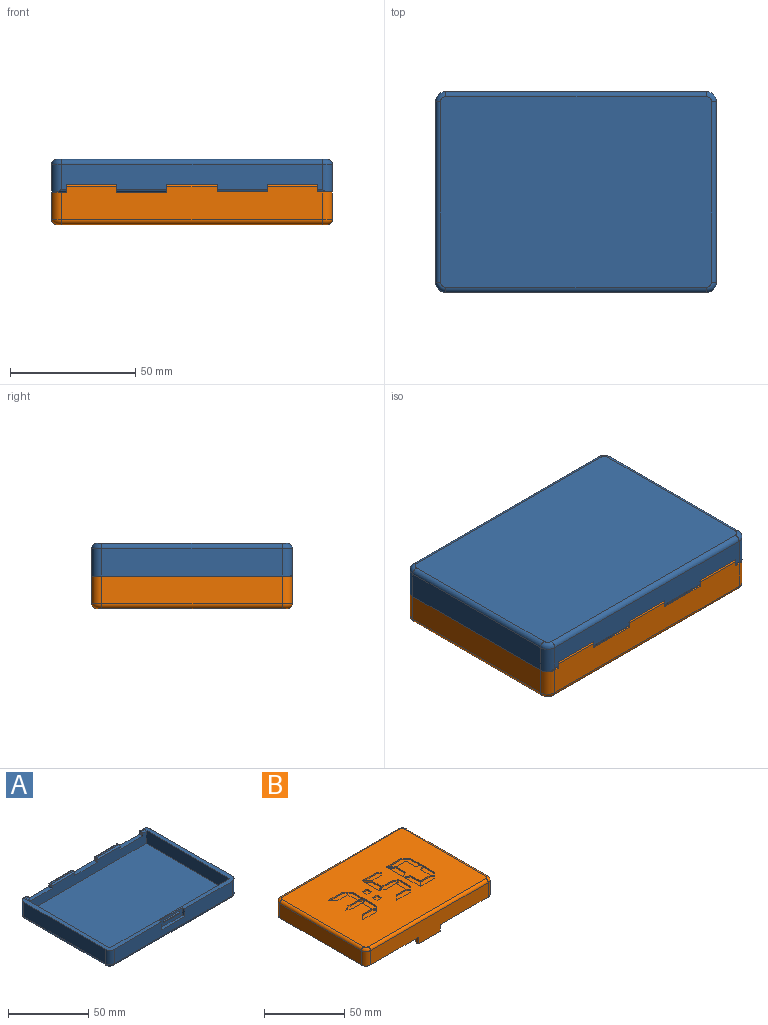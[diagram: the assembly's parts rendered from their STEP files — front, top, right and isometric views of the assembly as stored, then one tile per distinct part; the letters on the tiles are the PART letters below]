
ASSEMBLY  parts=2 mates=1
PART A: 63 faces, bbox 112.7x80.7x13 mm
  f0: plane 104x11mm, normal (0,-1,0), area 1024mm2, adj f1,f7,f8,f50,f54,f55,f62
  f1: plane 112x79mm, normal (0,0,1), area 748.6mm2, adj f0,f5,f6,f7,f8,f9,f10,f12
  f2: plane 20x1mm, normal (0,0,1), area 20mm2, adj f20,f24,f38,f41
  f3: plane 20x1mm, normal (0,0,1), area 20mm2, adj f17,f21,f39,f42
  f4: plane 104x10mm, normal (0,1,0), area 920mm2, adj f5,f10,f17,f18,f19,f20,f21,f22
  f5: cylinder r=4mm len=11mm, axis (0,0,-1), area 68mm2, adj f1,f4,f6,f45,f47
  f6: plane 72x11mm, normal (-1,0,0), area 792mm2, adj f1,f5,f7,f46
  f7: cylinder r=4mm len=11mm, axis (0,0,-1), area 69.1mm2, adj f0,f1,f6,f48
  f8: cylinder r=4mm len=11mm, axis (0,0,-1), area 69.1mm2, adj f0,f1,f9,f52
  f9: plane 72x11mm, normal (1,0,0), area 792mm2, adj f1,f8,f10,f53
  f10: cylinder r=4mm len=11mm, axis (0,0,-1), area 68mm2, adj f1,f4,f9,f44,f51
  f11: plane 108x76mm, normal (0,0,-1), area 8204.6mm2, adj f46,f47,f48,f49,f50,f51,f52,f53
  f12: plane 75x10mm, normal (-1,0,0), area 740.2mm2, adj f1,f13,f15,f16,f43
  f13: plane 106x9mm, normal (0,-1,0), area 834mm2, adj f12,f14,f16,f17,f18,f19,f20,f21
  f14: plane 75x10mm, normal (1,0,0), area 740.2mm2, adj f1,f13,f15,f16,f40
  f15: plane 106x10mm, normal (0,1,0), area 1060mm2, adj f1,f12,f14,f16
  f16: plane 106x74mm, normal (0,0,1), area 7844mm2, adj f12,f13,f14,f15
  f17: plane 3x3mm, normal (1,0,0), area 6.8mm2, adj f3,f4,f13,f19,f30,f39,f42
  f18: plane 3x3mm, normal (-1,0,0), area 6.8mm2, adj f1,f4,f13,f19,f36,f43,f44
  f19: plane 20x3mm, normal (0,0,1), area 60mm2, adj f4,f13,f17,f18
  f20: plane 3x3mm, normal (1,0,0), area 6.8mm2, adj f2,f4,f13,f22,f28,f38,f41
  f21: plane 3x3mm, normal (-1,0,0), area 6.8mm2, adj f3,f4,f13,f22,f34,f39,f42
  f22: plane 20x3mm, normal (0,0,1), area 60mm2, adj f4,f13,f20,f21
  f23: plane 3x3mm, normal (1,0,0), area 6.8mm2, adj f1,f4,f13,f25,f26,f40,f45
  f24: plane 3x3mm, normal (-1,0,0), area 6.8mm2, adj f2,f4,f13,f25,f32,f38,f41
  f25: plane 20x3mm, normal (0,0,1), area 60mm2, adj f4,f13,f23,f24
  f26: cylinder r=0.75mm len=1.5mm, axis (1,0,0), area 4.7mm2, adj f23,f27
  f27: plane 1.5x1.5mm, normal (1,0,0), area 1.8mm2, adj f26
  f28: cylinder r=0.75mm len=1.5mm, axis (1,0,0), area 7.1mm2, adj f20,f29
  f29: plane 1.5x1.5mm, normal (1,0,0), area 1.8mm2, adj f28
  f30: cylinder r=0.75mm len=1.5mm, axis (1,0,0), area 7.1mm2, adj f17,f31
  f31: plane 1.5x1.5mm, normal (1,0,0), area 1.8mm2, adj f30
  f32: cylinder r=0.75mm len=1.5mm, axis (-1,0,0), area 7.1mm2, adj f24,f33
  f33: plane 1.5x1.5mm, normal (-1,0,0), area 1.8mm2, adj f32
  f34: cylinder r=0.75mm len=1.5mm, axis (-1,0,0), area 7.1mm2, adj f21,f35
  f35: plane 1.5x1.5mm, normal (-1,0,0), area 1.8mm2, adj f34
  f36: cylinder r=0.75mm len=1.5mm, axis (-1,0,0), area 7.1mm2, adj f18,f37
  f37: plane 1.5x1.5mm, normal (-1,0,0), area 1.8mm2, adj f36
  f38: cylinder r=1mm len=20mm, axis (1,0,0), area 31.4mm2, adj f2,f4,f20,f24
  f39: cylinder r=1mm len=20mm, axis (1,0,0), area 31.4mm2, adj f3,f4,f17,f21
  f40: cylinder r=1mm len=3mm, axis (1,0,0), area 4.7mm2, adj f1,f13,f14,f23
  f41: cylinder r=1mm len=20mm, axis (1,0,0), area 31.4mm2, adj f2,f13,f20,f24
  f42: cylinder r=1mm len=20mm, axis (1,0,0), area 31.4mm2, adj f3,f13,f17,f21
  f43: cylinder r=1mm len=3mm, axis (1,0,0), area 4.7mm2, adj f1,f12,f13,f18
  f44: cylinder r=1mm len=4.65mm, axis (1,0,0), area 5.4mm2, adj f1,f4,f10,f18
  f45: cylinder r=1mm len=4.65mm, axis (1,0,0), area 5.4mm2, adj f1,f4,f5,f23
  f46: cylinder r=2mm len=72mm, axis (0,-1,0), area 226.2mm2, adj f6,f11,f47,f48
  f47: torus R=2mm, axis (0,0,1), area 16.2mm2, adj f5,f11,f46,f49
  f48: torus R=2mm, axis (0,0,1), area 16.2mm2, adj f7,f11,f46,f50
  f49: cylinder r=2mm len=104mm, axis (-1,0,0), area 326.7mm2, adj f4,f11,f47,f51
  f50: cylinder r=2mm len=104mm, axis (1,0,0), area 326.7mm2, adj f0,f11,f48,f52
  f51: torus R=2mm, axis (0,0,1), area 16.2mm2, adj f10,f11,f49,f53
  f52: torus R=2mm, axis (0,0,1), area 16.2mm2, adj f8,f11,f50,f53
  f53: cylinder r=2mm len=72mm, axis (0,1,0), area 226.2mm2, adj f9,f11,f51,f52
  f54: plane 6x2mm, normal (1,0,0), area 12mm2, adj f0,f1,f56,f62
  f55: plane 6x2mm, normal (-1,0,0), area 12mm2, adj f0,f1,f56,f62
  f56: plane 20x6mm, normal (0,-1,0), area 99mm2, adj f1,f54,f55,f58,f59,f60,f61,f62
  f57: plane 12.6x0.1mm, normal (0,-1,0), area 1.3mm2, adj f58,f59,f60,f61
  f58: cylinder r=0.7mm len=14mm, axis (1,0,0), area 14.8mm2, adj f56,f57,f59,f60
  f59: cylinder r=0.7mm len=1.5mm, axis (0,0,1), area 1.1mm2, adj f56,f57,f58,f61
  f60: cylinder r=0.7mm len=1.5mm, axis (0,0,-1), area 1.1mm2, adj f56,f57,f58,f61
  f61: cylinder r=0.7mm len=14mm, axis (-1,0,0), area 14.8mm2, adj f56,f57,f59,f60
  f62: plane 20x2mm, normal (0,0,1), area 40mm2, adj f0,f54,f55,f56
PART B: 177 faces, bbox 112.7x80.7x18 mm
  f0: plane 19.5x4mm, normal (0,1,0), area 38mm2, adj f1,f164,f165,f172,f173,f174,f175,f176
  f1: plane 112x80mm, normal (0,0,-1), area 763.3mm2, adj f0,f5,f6,f7,f8,f9,f10,f11
  f2: plane 108x76mm, normal (0,0,1), area 7443.8mm2, adj f51,f52,f53,f54,f55,f57,f58,f59
  f3: plane 20x3mm, normal (0,0,-1), area 60mm2, adj f5,f14,f22,f24
  f4: plane 20x3mm, normal (0,0,-1), area 60mm2, adj f5,f14,f19,f21
  f5: plane 106x12mm, normal (0,-1,0), area 1180mm2, adj f1,f3,f4,f6,f16,f17,f18,f19
  f6: plane 74x10mm, normal (1,0,0), area 740mm2, adj f1,f5,f7,f17
  f7: plane 106x10mm, normal (0,1,0), area 1060mm2, adj f1,f6,f16,f17
  f8: plane 72x11mm, normal (1,0,0), area 792mm2, adj f1,f9,f15,f160
  f9: cylinder r=4mm len=11mm, axis (0,0,1), area 69.1mm2, adj f1,f8,f10,f158
  f10: plane 104x16mm, normal (0,-1,0), area 1241.5mm2, adj f1,f9,f11,f156,f164,f165,f166
  f11: cylinder r=4mm len=11mm, axis (0,0,1), area 69.1mm2, adj f1,f10,f12,f157
  f12: plane 72x11mm, normal (-1,0,0), area 792mm2, adj f1,f11,f13,f159
  f13: cylinder r=4mm len=11mm, axis (0,0,1), area 69.1mm2, adj f1,f12,f14,f161
  f14: plane 104x13mm, normal (0,1,0), area 1264mm2, adj f1,f3,f4,f13,f15,f18,f19,f21
  f15: cylinder r=4mm len=11mm, axis (0,0,1), area 69.1mm2, adj f1,f8,f14,f162
  f16: plane 74x10mm, normal (-1,0,0), area 740mm2, adj f1,f5,f7,f17
  f17: plane 106x74mm, normal (0,0,-1), area 7844mm2, adj f5,f6,f7,f16
  f18: plane 3x3mm, normal (1,0,0), area 6.8mm2, adj f1,f5,f14,f20,f36,f49,f50
  f19: plane 3x3mm, normal (-1,0,0), area 6.8mm2, adj f4,f5,f14,f20,f27,f49,f50
  f20: plane 20x1mm, normal (0,0,-1), area 20mm2, adj f18,f19,f49,f50
  f21: plane 3x3mm, normal (1,0,0), area 6.8mm2, adj f4,f5,f14,f23,f38,f47,f48
  f22: plane 3x3mm, normal (-1,0,0), area 6.8mm2, adj f3,f5,f14,f23,f30,f47,f48
  f23: plane 20x1mm, normal (0,0,-1), area 20mm2, adj f21,f22,f47,f48
  f24: plane 3x3mm, normal (1,0,0), area 6.8mm2, adj f3,f5,f14,f26,f40,f45,f46
  f25: plane 3x3mm, normal (-1,0,0), area 6.8mm2, adj f1,f5,f14,f26,f32,f45,f46
  f26: plane 20x1mm, normal (0,0,-1), area 20mm2, adj f24,f25,f45,f46
  f27: cylinder r=0.75mm len=1.5mm, axis (1,0,0), area 0.9mm2, adj f19,f29
  f28: plane 0.5x0.5mm, normal (-1,0,0), area 0.2mm2, adj f29
  f29: torus R=0.25mm, axis (-1,0,0), area 2.8mm2, adj f27,f28
  f30: cylinder r=0.75mm len=1.5mm, axis (1,0,0), area 0.9mm2, adj f22,f34
  f31: plane 0.5x0.5mm, normal (-1,0,0), area 0.2mm2, adj f34
  f32: cylinder r=0.75mm len=1.5mm, axis (1,0,0), area 0.9mm2, adj f25,f35
  f33: plane 0.5x0.5mm, normal (-1,0,0), area 0.2mm2, adj f35
  f34: torus R=0.25mm, axis (-1,0,0), area 2.8mm2, adj f30,f31
  f35: torus R=0.25mm, axis (-1,0,0), area 2.8mm2, adj f32,f33
  f36: cylinder r=0.75mm len=1.5mm, axis (-1,0,0), area 0.9mm2, adj f18,f42
  f37: plane 0.5x0.5mm, normal (1,0,0), area 0.2mm2, adj f42
  f38: cylinder r=0.75mm len=1.5mm, axis (-1,0,0), area 0.9mm2, adj f21,f43
  f39: plane 0.5x0.5mm, normal (1,0,0), area 0.2mm2, adj f43
  f40: cylinder r=0.75mm len=1.5mm, axis (-1,0,0), area 0.9mm2, adj f24,f44
  f41: plane 0.5x0.5mm, normal (1,0,0), area 0.2mm2, adj f44
  f42: torus R=0.25mm, axis (1,0,0), area 2.8mm2, adj f36,f37
  f43: torus R=0.25mm, axis (1,0,0), area 2.8mm2, adj f38,f39
  f44: torus R=0.25mm, axis (1,0,0), area 2.8mm2, adj f40,f41
  f45: cylinder r=1mm len=20mm, axis (1,0,0), area 31.4mm2, adj f5,f24,f25,f26
  f46: cylinder r=1mm len=20mm, axis (-1,0,0), area 31.4mm2, adj f14,f24,f25,f26
  f47: cylinder r=1mm len=20mm, axis (1,0,0), area 31.4mm2, adj f5,f21,f22,f23
  f48: cylinder r=1mm len=20mm, axis (-1,0,0), area 31.4mm2, adj f14,f21,f22,f23
  f49: cylinder r=1mm len=20mm, axis (1,0,0), area 31.4mm2, adj f5,f18,f19,f20
  f50: cylinder r=1mm len=20mm, axis (-1,0,0), area 31.4mm2, adj f14,f18,f19,f20
  f51: plane 12.3x1mm, normal (0,-1,0), area 12.3mm2, adj f2,f52,f55,f56
  f52: plane 4.1x4.1mm, normal (0.71,0.71,0), area 5.8mm2, adj f2,f51,f53,f56
  f53: plane 8.2x1mm, normal (0,1,0), area 8.2mm2, adj f2,f52,f54,f56
  f54: plane 2.05x2.05mm, normal (-0.71,0.71,0), area 2.9mm2, adj f2,f53,f55,f56
  f55: plane 2.05x2.05mm, normal (-0.71,-0.71,0), area 2.9mm2, adj f2,f51,f54,f56
  f56: plane 14.35x4.1mm, normal (0,0,1), area 46.2mm2, adj f51,f52,f53,f54,f55
  f57: plane 4.1x2.05mm, normal (-0.45,-0.89,0), area 4.6mm2, adj f2,f58,f60,f61
  f58: plane 14.35x1mm, normal (1,0,0), area 14.4mm2, adj f2,f57,f59,f61
  f59: plane 4.1x4.1mm, normal (-0.71,0.71,0), area 5.8mm2, adj f2,f58,f60,f61
  f60: plane 8.2x1mm, normal (-1,0,0), area 8.2mm2, adj f2,f57,f59,f61
  f61: plane 14.35x4.1mm, normal (0,0,1), area 46.2mm2, adj f57,f58,f59,f60
  f62: plane 8.2x1mm, normal (1,0,0), area 8.2mm2, adj f2,f63,f66,f67
  f63: plane 2.04x2.04mm, normal (0.71,0.71,0), area 2.9mm2, adj f2,f62,f64,f67
  f64: plane 2.06x2.04mm, normal (-0.7,0.71,0), area 2.9mm2, adj f2,f63,f65,f67
  f65: plane 10.25x1mm, normal (-1,0,0), area 10.3mm2, adj f2,f64,f66,f67
  f66: plane 4.1x2.05mm, normal (0.45,-0.89,0), area 4.6mm2, adj f2,f62,f65,f67
  f67: plane 12.3x4.1mm, normal (0,0,1), area 42mm2, adj f62,f63,f64,f65,f66
  f68: plane 4.1x4.1mm, normal (0.71,-0.71,0), area 5.8mm2, adj f2,f69,f72,f73
  f69: plane 12.3x1mm, normal (0,1,0), area 12.3mm2, adj f2,f68,f70,f73
  f70: plane 2.05x2.05mm, normal (-0.71,0.71,0), area 2.9mm2, adj f2,f69,f71,f73
  f71: plane 2.05x2.05mm, normal (-0.71,-0.71,0), area 2.9mm2, adj f2,f70,f72,f73
  f72: plane 8.2x1mm, normal (0,-1,0), area 8.2mm2, adj f2,f68,f71,f73
  f73: plane 14.35x4.1mm, normal (0,0,1), area 46.2mm2, adj f68,f69,f70,f71,f72
  f74: plane 2.04x2.04mm, normal (0.71,-0.71,0), area 2.9mm2, adj f2,f75,f78,f79
  f75: plane 8.2x1mm, normal (1,0,0), area 8.2mm2, adj f2,f74,f76,f79
  f76: plane 4.1x2.05mm, normal (0.45,0.89,0), area 4.6mm2, adj f2,f75,f77,f79
  f77: plane 10.25x1mm, normal (-1,0,0), area 10.3mm2, adj f2,f76,f78,f79
  f78: plane 2.06x2.04mm, normal (-0.7,-0.71,0), area 2.9mm2, adj f2,f74,f77,f79
  f79: plane 12.3x4.1mm, normal (0,0,1), area 42mm2, adj f74,f75,f76,f77,f78
  f80: plane 4.1x2.05mm, normal (0.45,-0.89,0), area 4.6mm2, adj f2,f81,f85,f86
  f81: plane 4.1x2.05mm, normal (0.45,0.89,0), area 4.6mm2, adj f2,f80,f82,f86
  f82: plane 8.2x1mm, normal (0,1,0), area 8.2mm2, adj f2,f81,f83,f86
  f83: plane 4.1x2.05mm, normal (-0.45,0.89,0), area 4.6mm2, adj f2,f82,f84,f86
  f84: plane 4.1x2.05mm, normal (-0.45,-0.89,0), area 4.6mm2, adj f2,f83,f85,f86
  f85: plane 8.2x1mm, normal (0,-1,0), area 8.2mm2, adj f2,f80,f84,f86
  f86: plane 16.4x4.1mm, normal (0,0,1), area 50.4mm2, adj f80,f81,f82,f83,f84,f85
  f87: plane 4.1x1mm, normal (0,-1,0), area 4.1mm2, adj f2,f88,f90,f91
  f88: plane 4.1x1mm, normal (1,0,0), area 4.1mm2, adj f2,f87,f89,f91
  f89: plane 4.1x1mm, normal (0,1,0), area 4.1mm2, adj f2,f88,f90,f91
  f90: plane 4.1x1mm, normal (-1,0,0), area 4.1mm2, adj f2,f87,f89,f91
  f91: plane 4.1x4.1mm, normal (0,0,1), area 16.8mm2, adj f87,f88,f89,f90
  f92: plane 4.1x1mm, normal (0,-1,0), area 4.1mm2, adj f2,f93,f95,f96
  f93: plane 4.1x1mm, normal (1,0,0), area 4.1mm2, adj f2,f92,f94,f96
  f94: plane 4.1x1mm, normal (0,1,0), area 4.1mm2, adj f2,f93,f95,f96
  f95: plane 4.1x1mm, normal (-1,0,0), area 4.1mm2, adj f2,f92,f94,f96
  f96: plane 4.1x4.1mm, normal (0,0,1), area 16.8mm2, adj f92,f93,f94,f95
  f97: plane 4.1x4.1mm, normal (-0.71,-0.71,0), area 5.8mm2, adj f2,f98,f100,f101
  f98: plane 14.35x1mm, normal (1,0,0), area 14.4mm2, adj f2,f97,f99,f101
  f99: plane 4.1x2.05mm, normal (-0.45,0.89,0), area 4.6mm2, adj f2,f98,f100,f101
  f100: plane 8.2x1mm, normal (-1,0,0), area 8.2mm2, adj f2,f97,f99,f101
  f101: plane 14.35x4.1mm, normal (0,0,1), area 46.2mm2, adj f97,f98,f99,f100
  f102: plane 12.3x1mm, normal (0,-1,0), area 12.3mm2, adj f2,f103,f106,f107
  f103: plane 4.1x4.1mm, normal (0.71,0.71,0), area 5.8mm2, adj f2,f102,f104,f107
  f104: plane 8.2x1mm, normal (0,1,0), area 8.2mm2, adj f2,f103,f105,f107
  f105: plane 2.05x2.05mm, normal (-0.71,0.71,0), area 2.9mm2, adj f2,f104,f106,f107
  f106: plane 2.05x2.05mm, normal (-0.71,-0.71,0), area 2.9mm2, adj f2,f102,f105,f107
  f107: plane 14.35x4.1mm, normal (0,0,1), area 46.2mm2, adj f102,f103,f104,f105,f106
  f108: plane 8.2x1mm, normal (1,0,0), area 8.2mm2, adj f2,f109,f112,f113
  f109: plane 2.04x2.04mm, normal (0.71,0.71,0), area 2.9mm2, adj f2,f108,f110,f113
  f110: plane 2.06x2.04mm, normal (-0.7,0.71,0), area 2.9mm2, adj f2,f109,f111,f113
  f111: plane 10.25x1mm, normal (-1,0,0), area 10.3mm2, adj f2,f110,f112,f113
  f112: plane 4.1x2.05mm, normal (0.45,-0.89,0), area 4.6mm2, adj f2,f108,f111,f113
  f113: plane 12.3x4.1mm, normal (0,0,1), area 42mm2, adj f108,f109,f110,f111,f112
  f114: plane 4.1x4.1mm, normal (0.71,-0.71,0), area 5.8mm2, adj f2,f115,f118,f119
  f115: plane 12.3x1mm, normal (0,1,0), area 12.3mm2, adj f2,f114,f116,f119
  f116: plane 2.05x2.05mm, normal (-0.71,0.71,0), area 2.9mm2, adj f2,f115,f117,f119
  f117: plane 2.05x2.05mm, normal (-0.71,-0.71,0), area 2.9mm2, adj f2,f116,f118,f119
  f118: plane 8.2x1mm, normal (0,-1,0), area 8.2mm2, adj f2,f114,f117,f119
  f119: plane 14.35x4.1mm, normal (0,0,1), area 46.2mm2, adj f114,f115,f116,f117,f118
  f120: plane 12.3x1mm, normal (0,-1,0), area 12.3mm2, adj f2,f121,f124,f125
  f121: plane 4.1x4.1mm, normal (0.71,0.71,0), area 5.8mm2, adj f2,f120,f122,f125
  f122: plane 8.2x1mm, normal (0,1,0), area 8.2mm2, adj f2,f121,f123,f125
  f123: plane 2.05x2.05mm, normal (-0.71,0.71,0), area 2.9mm2, adj f2,f122,f124,f125
  f124: plane 2.05x2.05mm, normal (-0.71,-0.71,0), area 2.9mm2, adj f2,f120,f123,f125
  f125: plane 14.35x4.1mm, normal (0,0,1), area 46.2mm2, adj f120,f121,f122,f123,f124
  f126: plane 2.04x2.04mm, normal (0.71,-0.71,0), area 2.9mm2, adj f2,f127,f130,f131
  f127: plane 8.2x1mm, normal (1,0,0), area 8.2mm2, adj f2,f126,f128,f131
  f128: plane 4.1x2.05mm, normal (0.45,0.89,0), area 4.6mm2, adj f2,f127,f129,f131
  f129: plane 10.25x1mm, normal (-1,0,0), area 10.3mm2, adj f2,f128,f130,f131
  f130: plane 2.06x2.04mm, normal (-0.7,-0.71,0), area 2.9mm2, adj f2,f126,f129,f131
  f131: plane 12.3x4.1mm, normal (0,0,1), area 42mm2, adj f126,f127,f128,f129,f130
  f132: plane 8.2x1mm, normal (1,0,0), area 8.2mm2, adj f2,f133,f136,f137
  f133: plane 2.04x2.04mm, normal (0.71,0.71,0), area 2.9mm2, adj f2,f132,f134,f137
  f134: plane 2.06x2.04mm, normal (-0.7,0.71,0), area 2.9mm2, adj f2,f133,f135,f137
  f135: plane 10.25x1mm, normal (-1,0,0), area 10.3mm2, adj f2,f134,f136,f137
  f136: plane 4.1x2.05mm, normal (0.45,-0.89,0), area 4.6mm2, adj f2,f132,f135,f137
  f137: plane 12.3x4.1mm, normal (0,0,1), area 42mm2, adj f132,f133,f134,f135,f136
  f138: plane 4.1x2.05mm, normal (0.45,-0.89,0), area 4.6mm2, adj f2,f139,f143,f144
  f139: plane 4.1x2.05mm, normal (0.45,0.89,0), area 4.6mm2, adj f2,f138,f140,f144
  f140: plane 8.2x1mm, normal (0,1,0), area 8.2mm2, adj f2,f139,f141,f144
  f141: plane 4.1x2.05mm, normal (-0.45,0.89,0), area 4.6mm2, adj f2,f140,f142,f144
  f142: plane 4.1x2.05mm, normal (-0.45,-0.89,0), area 4.6mm2, adj f2,f141,f143,f144
  f143: plane 8.2x1mm, normal (0,-1,0), area 8.2mm2, adj f2,f138,f142,f144
  f144: plane 16.4x4.1mm, normal (0,0,1), area 50.4mm2, adj f138,f139,f140,f141,f142,f143
  f145: plane 4.1x4.1mm, normal (0.71,-0.71,0), area 5.8mm2, adj f2,f146,f149,f150
  f146: plane 12.3x1mm, normal (0,1,0), area 12.3mm2, adj f2,f145,f147,f150
  f147: plane 2.05x2.05mm, normal (-0.71,0.71,0), area 2.9mm2, adj f2,f146,f148,f150
  f148: plane 2.05x2.05mm, normal (-0.71,-0.71,0), area 2.9mm2, adj f2,f147,f149,f150
  f149: plane 8.2x1mm, normal (0,-1,0), area 8.2mm2, adj f2,f145,f148,f150
  f150: plane 14.35x4.1mm, normal (0,0,1), area 46.2mm2, adj f145,f146,f147,f148,f149
  f151: plane 4.1x4.1mm, normal (-0.71,-0.71,0), area 5.8mm2, adj f2,f152,f154,f155
  f152: plane 14.35x1mm, normal (1,0,0), area 14.4mm2, adj f2,f151,f153,f155
  f153: plane 4.1x2.05mm, normal (-0.45,0.89,0), area 4.6mm2, adj f2,f152,f154,f155
  f154: plane 8.2x1mm, normal (-1,0,0), area 8.2mm2, adj f2,f151,f153,f155
  f155: plane 14.35x4.1mm, normal (0,0,1), area 46.2mm2, adj f151,f152,f153,f154
  f156: cylinder r=2mm len=104mm, axis (-1,0,0), area 326.7mm2, adj f2,f10,f157,f158
  f157: torus R=2mm, axis (0,0,-1), area 16.2mm2, adj f2,f11,f156,f159
  f158: torus R=2mm, axis (0,0,-1), area 16.2mm2, adj f2,f9,f156,f160
  f159: cylinder r=2mm len=72mm, axis (0,1,0), area 226.2mm2, adj f2,f12,f157,f161
  f160: cylinder r=2mm len=72mm, axis (0,-1,0), area 226.2mm2, adj f2,f8,f158,f162
  f161: torus R=2mm, axis (0,0,-1), area 16.2mm2, adj f2,f13,f159,f163
  f162: torus R=2mm, axis (0,0,-1), area 16.2mm2, adj f2,f15,f160,f163
  f163: cylinder r=2mm len=104mm, axis (1,0,0), area 326.7mm2, adj f2,f14,f161,f162
  f164: plane 5x2mm, normal (-1,0,0), area 9.8mm2, adj f0,f1,f10,f166,f176
  f165: plane 5x2mm, normal (1,0,0), area 9.8mm2, adj f0,f1,f10,f166,f176
  f166: plane 19.5x1mm, normal (0,0,-1), area 19.5mm2, adj f10,f164,f165,f176
  f167: plane 1.5x0.3mm, normal (-1,0,0), area 0.5mm2, adj f168,f170,f171,f172
  f168: plane 15x0.3mm, normal (0,0,1), area 4.5mm2, adj f167,f169,f171,f173
  f169: plane 1.5x0.3mm, normal (1,0,0), area 0.5mm2, adj f168,f170,f171,f175
  f170: plane 15x0.3mm, normal (0,0,-1), area 4.5mm2, adj f167,f169,f171,f174
  f171: plane 15x1.5mm, normal (0,1,0), area 22.5mm2, adj f167,f168,f169,f170
  f172: cylinder r=0.5mm len=2.5mm, axis (0,0,-1), area 1.5mm2, adj f0,f167,f173,f174
  f173: cylinder r=0.5mm len=16mm, axis (-1,0,0), area 12.1mm2, adj f0,f168,f172,f175
  f174: cylinder r=0.5mm len=16mm, axis (1,0,0), area 12.1mm2, adj f0,f170,f172,f175
  f175: cylinder r=0.5mm len=2.5mm, axis (0,0,1), area 1.5mm2, adj f0,f169,f173,f174
  f176: bspline ~21.45x1mm, area 31.7mm2, adj f0,f164,f165,f166
PLACE A rot(axis=(1,0,0),180deg) t=(-104,-80,46)mm
PLACE B rot(axis=(1,0,0),180deg) t=(-104,-80,26)mm
MATE fastened B.f1 <-> A.f1  axis (0,0,1) through (-52,-40,33)mm
